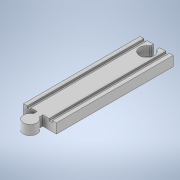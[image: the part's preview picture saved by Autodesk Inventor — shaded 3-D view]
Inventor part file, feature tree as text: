
AUTODESK INVENTOR PART (.ipt)
format: ipt  version: 2020 (Build 240168000, 168)  size: 143,872 bytes
history: native  units: in
note: dims shown in document units (in); Inventor stores cm internally (conversion verified against a paired STEP export)
features: sketch x2, extrude x2, plane x1, mirror x1, projected_geometry x1
ambient origin geometry x8: Origin, YZ Plane, XZ Plane, XY Plane, X Axis, Y Axis, Z Axis, Center Point
bodies: Solid1 (feature_tree)
feature tree (7):
  sketch  "Sketch1"  dims[d0=12.0in d1=3.4in]
  extrude  "Extrusion1"  Depth=3.4in
  extrude  "Extrusion2"  Depth=1.0in
  plane  "Work Plane1"
  mirror  "Mirror1"
  sketch  "Sketch2"  dims[d2=1.5in d3=1.0in d4=1.7in d7=0.125in d8=1.4in d9=1.0in d10=1.7in d12=0.3in d13=1.7in d14=1.0in d15=0.0in d16=0.1875in d17=0.35in d18=0.4in d19=12.0in d20=0.0in]
  projected_geometry  "Projected Loop1"
